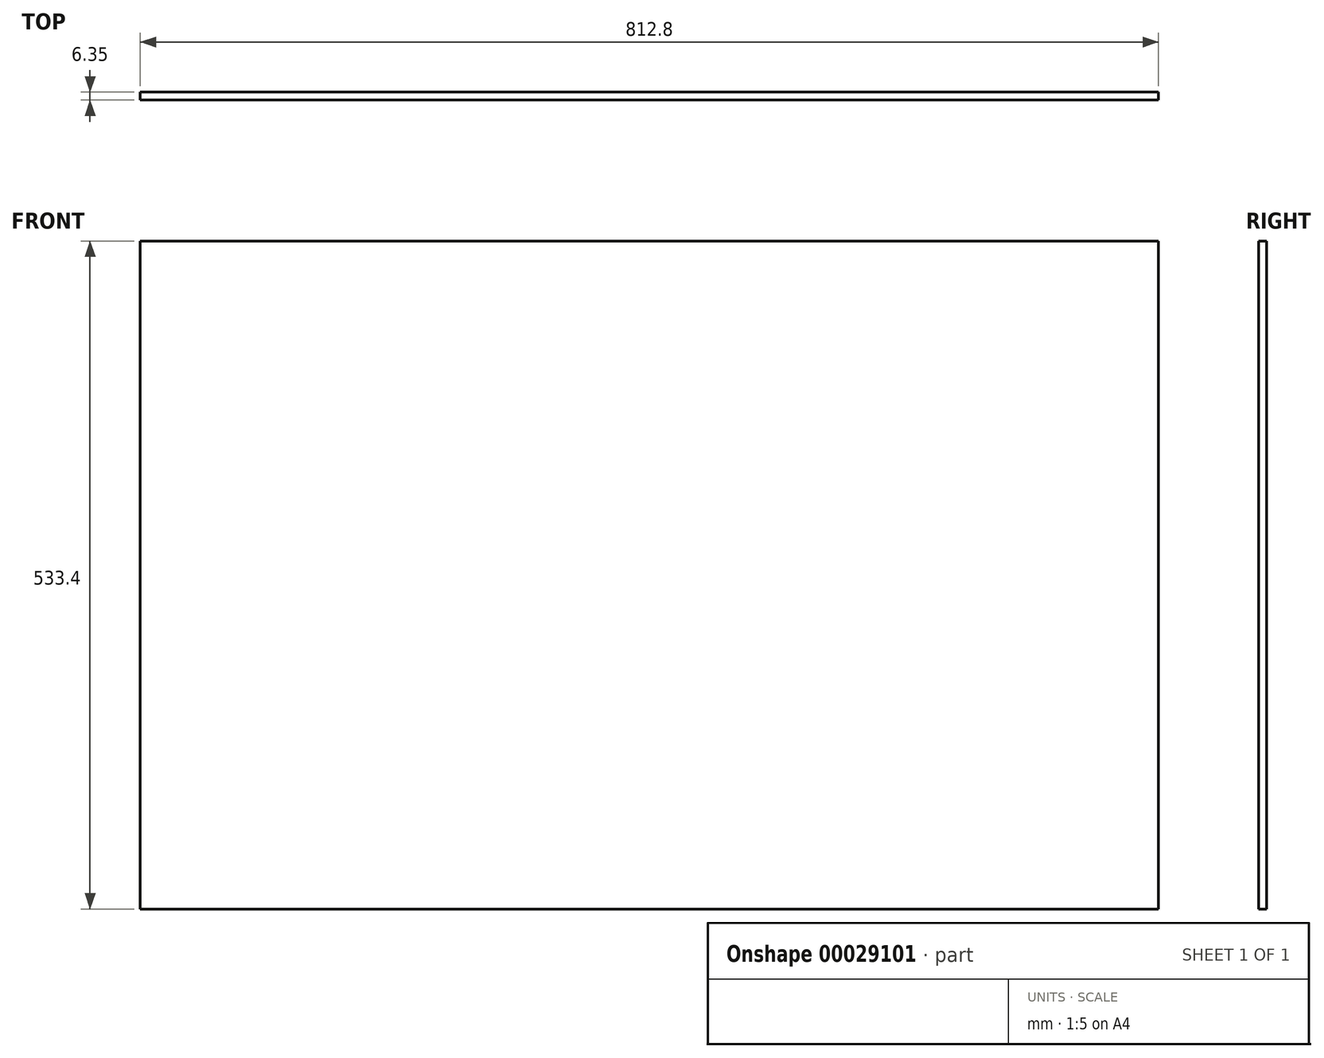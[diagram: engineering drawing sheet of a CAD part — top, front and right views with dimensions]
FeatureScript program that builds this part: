
annotation { "Feature Type Name" : "Feature", "Feature Type Description" : "" }
export const myFeature = defineFeature(function(context is Context, id is Id, definition is map)
    precondition{}
    {
        {
            var Q0;
            Q0=qCreatedBy(makeId("Front.planeOp"),FACE);
            var sketch = newSketch(context, id + "F0", { "sketchPlane" : qUnion([Q0])});
            skLineSegment(sketch, "E0.bottom", {"start": v(0, 533.4) * mm, "end": v(812.8, 533.4) * mm});
            skLineSegment(sketch, "E0.top", {"start": v(0, 0) * mm, "end": v(812.8, 0) * mm});
            skLineSegment(sketch, "E0.left", {"start": v(0, 533.4) * mm, "end": v(0, 0) * mm});
            skLineSegment(sketch, "E0.right", {"start": v(812.8, 533.4) * mm, "end": v(812.8, 0) * mm});
            skSolve(sketch);
        }
        {
            var Q0;
            Q0 = qSketchRegion(id + "F0", true);
            extrude(context, id + "F1", {"entities" : qUnion([Q0]), "depth" : 6.35 * mm});
        }
    });
